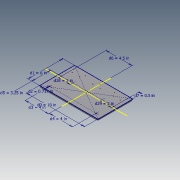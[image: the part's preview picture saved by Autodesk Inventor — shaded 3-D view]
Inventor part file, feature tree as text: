
AUTODESK INVENTOR PART (.ipt)
format: ipt  version: 2020.3 (Build 243373000, 373)  size: 145,408 bytes
history: native  units: in
note: dims shown in document units (in); Inventor stores cm internally (conversion verified against a paired STEP export)
features: hole x3, sketch x2, pattern_linear x2, extrude x1, fillet x1
ambient origin geometry x8: Origin, YZ Plane, XZ Plane, XY Plane, X Axis, Y Axis, Z Axis, Center Point
bodies: Solid1 (feature_tree)
feature tree (9):
  sketch  "Sketch1"  dims[d0=10.0in d1=6.0in]
  extrude  "Extrusion1"  Depth=6.0in
  hole  "Hole1"  [1 undecoded]
  hole  "Hole2"  [1 undecoded]
  pattern_linear  "Rectangular Pattern1"  Spacing1=3.25in  [1 undecoded]
  hole  "Hole3"  [1 undecoded]
  fillet  "Fillet1"  Radius=0.5in
  pattern_linear  "Rectangular Pattern2"  Spacing1=0.23in  [1 undecoded]
  sketch  "Sketch2"  dims[d2=0.737in d3=4.0in d4=4.0in d5=3.25in d6=4.5in d7=0.5in d8=0.23in d9=0.0in d10=0.255in d11=0.75in d12=0.375in d13=0.25in d14=0.5635in d15=1.0in d16=0.8108in d17=0.123in d18=0.75in d19=0.375in d20=0.25in d21=0.5635in d22=1.0in d23=0.8108in d24=0.7874in d26=2.125in d27=0.25in d28=2.0in d29=2.0in d31=1.25in d32=0.625in d33=0.625in d34=0.123in d35=0.75in d36=0.375in d37=0.25in d38=0.5635in d39=1.0in d40=0.8108in d41=1.1811in d43=3.5in]
note: 5 required parameter values undecoded (feature->parameter linkage not recoverable at this tier; creation-order binding heuristic only, values carry confidence <= 0.55)
